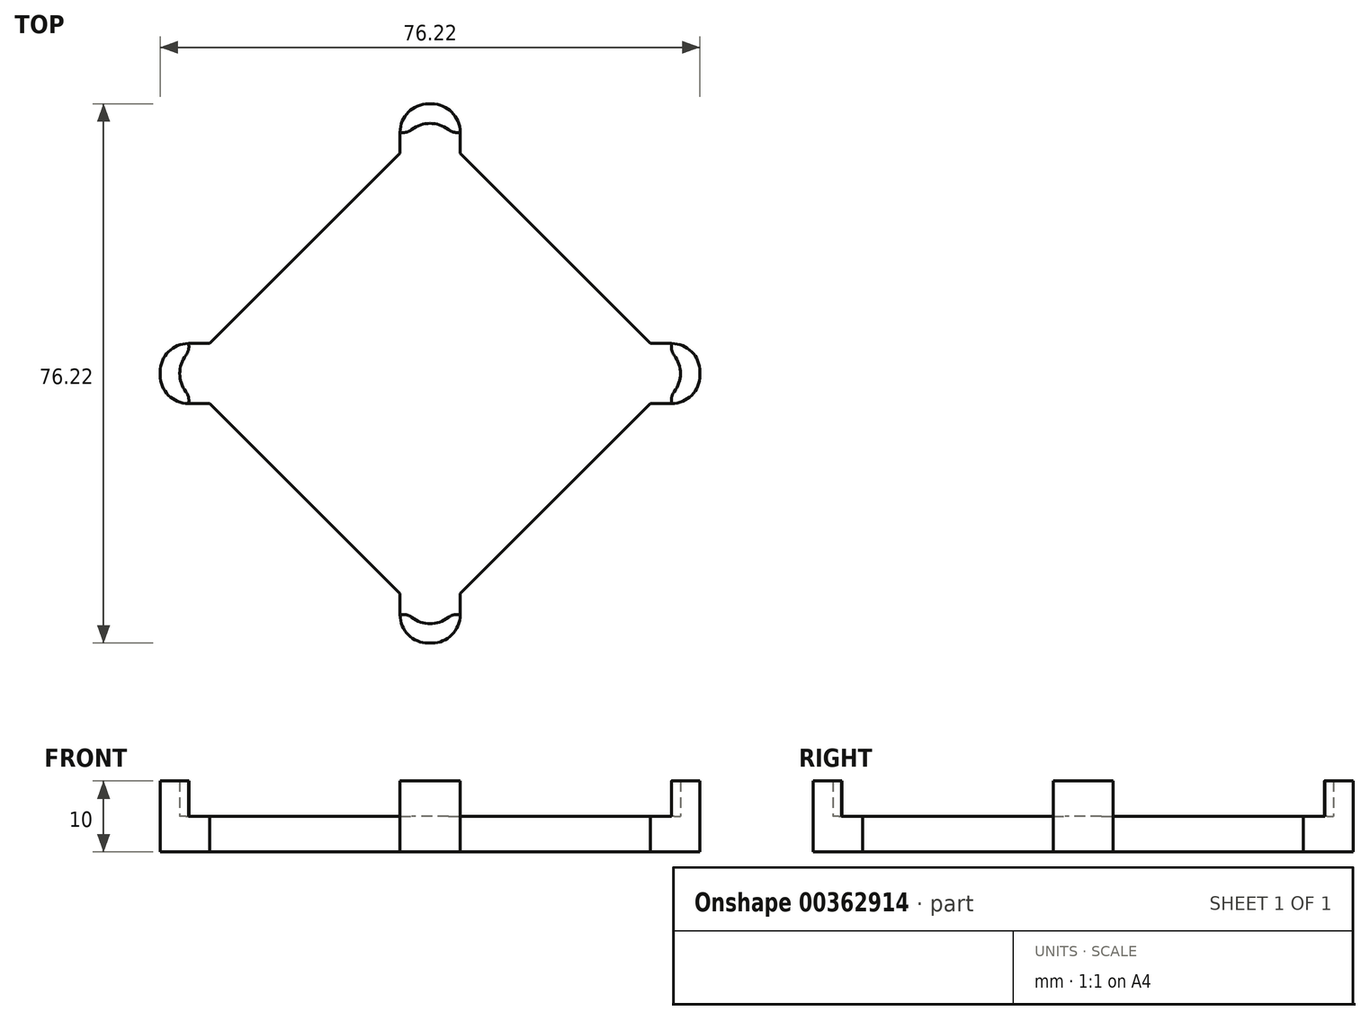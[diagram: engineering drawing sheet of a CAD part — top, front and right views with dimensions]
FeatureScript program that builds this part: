
annotation { "Feature Type Name" : "Feature", "Feature Type Description" : "" }
export const myFeature = defineFeature(function(context is Context, id is Id, definition is map)
    precondition{}
    {
        {
            var Q0;
            Q0=qCreatedBy(makeId("Top.planeOp"),FACE);
            var sketch = newSketch(context, id + "F0", { "sketchPlane" : qUnion([Q0])});
            skLineSegment(sketch, "E0", {"start": v(0, 35.36) * mm, "end": v(0, -35.36) * mm, "construction": true});
            skLineSegment(sketch, "E1", {"start": v(-35.36, 0) * mm, "end": v(35.36, 0) * mm, "construction": true});
            skPoint(sketch, "E2", {"position": v(0, 27.5) * mm});
            skPoint(sketch, "E3", {"position": v(-27.5, 0) * mm});
            skPoint(sketch, "E4", {"position": v(0, -27.5) * mm});
            skPoint(sketch, "E5", {"position": v(27.5, 0) * mm});
            skPoint(sketch, "E6", {"position": v(0, 0) * mm});
            skPoint(sketch, "E7", {"position": v(4.24, 31.11) * mm});
            skPoint(sketch, "E8", {"position": v(-4.24, 31.11) * mm});
            skPoint(sketch, "E9", {"position": v(-8.56, 26.8) * mm});
            skPoint(sketch, "E10", {"position": v(8.56, 26.8) * mm});
            skPoint(sketch, "E11", {"position": v(31.11, 4.24) * mm});
            skPoint(sketch, "E12", {"position": v(31.11, -4.24) * mm});
            skPoint(sketch, "E13", {"position": v(26.8, 8.56) * mm});
            skPoint(sketch, "E14", {"position": v(-31.11, -4.24) * mm});
            skPoint(sketch, "E15", {"position": v(-31.11, 4.24) * mm});
            skPoint(sketch, "E16", {"position": v(-26.8, 8.56) * mm});
            skPoint(sketch, "E17", {"position": v(4.24, -31.11) * mm});
            skPoint(sketch, "E18", {"position": v(-4.24, -31.11) * mm});
            skLineSegment(sketch, "E19", {"start": v(-31.11, 4.24) * mm, "end": v(-4.24, 31.11) * mm});
            skLineSegment(sketch, "E20", {"start": v(4.24, 31.11) * mm, "end": v(31.11, 4.24) * mm});
            skLineSegment(sketch, "E21", {"start": v(31.11, -4.24) * mm, "end": v(4.24, -31.11) * mm});
            skLineSegment(sketch, "E22", {"start": v(-4.24, -31.11) * mm, "end": v(-31.11, -4.24) * mm});
            skPoint(sketch, "E23", {"position": v(-17.68, -17.68) * mm});
            skPoint(sketch, "E24", {"position": v(17.68, -17.68) * mm});
            skPoint(sketch, "E25", {"position": v(17.68, 17.68) * mm});
            skPoint(sketch, "E26", {"position": v(-17.68, 17.68) * mm});
            skLineSegment(sketch, "E27", {"start": v(31.11, 4.24) * mm, "end": v(38.11, 4.24) * mm});
            skLineSegment(sketch, "E28", {"start": v(38.11, 4.24) * mm, "end": v(38.11, -4.24) * mm});
            skLineSegment(sketch, "E29", {"start": v(38.11, -4.24) * mm, "end": v(31.11, -4.24) * mm});
            skLineSegment(sketch, "E30", {"start": v(4.24, -31.11) * mm, "end": v(4.24, -38.11) * mm});
            skLineSegment(sketch, "E31", {"start": v(4.24, -38.11) * mm, "end": v(-4.24, -38.11) * mm});
            skLineSegment(sketch, "E32", {"start": v(-4.24, -38.11) * mm, "end": v(-4.24, -31.11) * mm});
            skLineSegment(sketch, "E33", {"start": v(-31.11, -4.24) * mm, "end": v(-38.11, -4.24) * mm});
            skLineSegment(sketch, "E34", {"start": v(-38.11, -4.24) * mm, "end": v(-38.11, 4.24) * mm});
            skLineSegment(sketch, "E35", {"start": v(-38.11, 4.24) * mm, "end": v(-31.11, 4.24) * mm});
            skLineSegment(sketch, "E36", {"start": v(-4.24, 31.11) * mm, "end": v(-4.24, 38.11) * mm});
            skLineSegment(sketch, "E37", {"start": v(-4.24, 38.11) * mm, "end": v(4.24, 38.11) * mm});
            skLineSegment(sketch, "E38", {"start": v(4.24, 38.11) * mm, "end": v(4.24, 31.11) * mm});
            skLineSegment(sketch, "E39", {"start": v(-4.24, -31.11) * mm, "end": v(4.24, -31.11) * mm});
            skLineSegment(sketch, "E40", {"start": v(31.11, -4.24) * mm, "end": v(31.11, 4.24) * mm});
            skLineSegment(sketch, "E41", {"start": v(4.24, 31.11) * mm, "end": v(-4.24, 31.11) * mm});
            skLineSegment(sketch, "E42", {"start": v(-31.11, 4.24) * mm, "end": v(-31.11, -4.24) * mm});
            skArc(sketch, "E43", {"start": v(-4.24, -31.11) * mm, "mid": v(0, -35.36) * mm, "end": v(4.24, -31.11) * mm});
            skArc(sketch, "E44", {"start": v(31.11, -4.24) * mm, "mid": v(35.36, 0) * mm, "end": v(31.11, 4.24) * mm});
            skArc(sketch, "E45", {"start": v(4.24, 31.11) * mm, "mid": v(0, 35.36) * mm, "end": v(-4.24, 31.11) * mm});
            skArc(sketch, "E46", {"start": v(-31.11, 4.24) * mm, "mid": v(-35.36, 0) * mm, "end": v(-31.11, -4.24) * mm});
            skSolve(sketch);
        }
        {
            var Q0;
            Q0=makeQuery(id+"F0.imprint","IMPRINT",FACE,{"disambiguationData":[TD([[makeQuery(id+"F0.imprint","IMPRINT",EDGE,{"derivedFrom":sQuery(id+"F0.wireOp",EDGE,"E39")}),-1.0]])]});
            var Q1;
            Q1=makeQuery(id+"F0.imprint","IMPRINT",FACE,{"disambiguationData":[TD([[makeQuery(id+"F0.imprint","IMPRINT",EDGE,{"derivedFrom":sQuery(id+"F0.wireOp",EDGE,"E19")}),-1.0]])]});
            var Q2;
            Q2=makeQuery(id+"F0.imprint","IMPRINT",FACE,{"disambiguationData":[TD([[makeQuery(id+"F0.imprint","IMPRINT",EDGE,{"derivedFrom":sQuery(id+"F0.wireOp",EDGE,"E42")}),-1.0]])]});
            var Q3;
            Q3=makeQuery(id+"F0.imprint","IMPRINT",FACE,{"disambiguationData":[TD([[makeQuery(id+"F0.imprint","IMPRINT",EDGE,{"derivedFrom":sQuery(id+"F0.wireOp",EDGE,"E40")}),-1.0]])]});
            var Q4;
            Q4=makeQuery(id+"F0.imprint","IMPRINT",FACE,{"disambiguationData":[TD([[makeQuery(id+"F0.imprint","IMPRINT",EDGE,{"derivedFrom":sQuery(id+"F0.wireOp",EDGE,"E27")}),-1.0]])]});
            var Q5;
            Q5=makeQuery(id+"F0.imprint","IMPRINT",FACE,{"disambiguationData":[TD([[makeQuery(id+"F0.imprint","IMPRINT",EDGE,{"derivedFrom":sQuery(id+"F0.wireOp",EDGE,"E30")}),-1.0]])]});
            var Q6;
            Q6=makeQuery(id+"F0.imprint","IMPRINT",FACE,{"disambiguationData":[TD([[makeQuery(id+"F0.imprint","IMPRINT",EDGE,{"derivedFrom":sQuery(id+"F0.wireOp",EDGE,"E33")}),-1.0]])]});
            var Q7;
            Q7=makeQuery(id+"F0.imprint","IMPRINT",FACE,{"disambiguationData":[TD([[makeQuery(id+"F0.imprint","IMPRINT",EDGE,{"derivedFrom":sQuery(id+"F0.wireOp",EDGE,"E41")}),-1.0]])]});
            var Q8;
            Q8=makeQuery(id+"F0.imprint","IMPRINT",FACE,{"disambiguationData":[TD([[makeQuery(id+"F0.imprint","IMPRINT",EDGE,{"derivedFrom":sQuery(id+"F0.wireOp",EDGE,"E36")}),-1.0]])]});
            extrude(context, id + "F1", {"entities" : qUnion([Q0, Q1, Q2, Q3, Q4, Q5, Q6, Q7, Q8]), "oppositeDirection" : true, "depth" : 5 * mm, "offsetDistance" : 25 * mm});
        }
        {
            var Q0;
            Q0=makeQuery(id+"F0.imprint","IMPRINT",FACE,{"disambiguationData":[TD([[makeQuery(id+"F0.imprint","IMPRINT",EDGE,{"derivedFrom":sQuery(id+"F0.wireOp",EDGE,"E33")}),-1.0]])]});
            var Q1;
            Q1=makeQuery(id+"F0.imprint","IMPRINT",FACE,{"disambiguationData":[TD([[makeQuery(id+"F0.imprint","IMPRINT",EDGE,{"derivedFrom":sQuery(id+"F0.wireOp",EDGE,"E30")}),-1.0]])]});
            var Q2;
            Q2=makeQuery(id+"F0.imprint","IMPRINT",FACE,{"disambiguationData":[TD([[makeQuery(id+"F0.imprint","IMPRINT",EDGE,{"derivedFrom":sQuery(id+"F0.wireOp",EDGE,"E36")}),-1.0]])]});
            var Q3;
            Q3=makeQuery(id+"F0.imprint","IMPRINT",FACE,{"disambiguationData":[TD([[makeQuery(id+"F0.imprint","IMPRINT",EDGE,{"derivedFrom":sQuery(id+"F0.wireOp",EDGE,"E27")}),-1.0]])]});
            extrude(context, id + "F2", {"entities" : qUnion([Q0, Q1, Q2, Q3]), "operationType" : NewBodyOperationType.ADD, "depth" : 5 * mm, "offsetDistance" : 25 * mm});
        }
        {
            var Q0;
            {var subQ0=sQuery(id+"F0.wireOp",EDGE,"E38");var subQ1=sQuery(id+"F0.wireOp",EDGE,"E37");Q0=makeQuery(id+"F2.boolean.opBoolean","MERGE",EDGE,{"derivedFrom":[makeQuery(id+"F1.opExtrude","SWEPT_EDGE",EDGE,{"disambiguationData":[OSD([subQ1,subQ0])]}),makeQuery(id+"F2.opExtrude","SWEPT_EDGE",EDGE,{"disambiguationData":[OSD([subQ1,subQ0])]})]});}
            var Q1;
            {var subQ0=sQuery(id+"F0.wireOp",EDGE,"E37");var subQ1=sQuery(id+"F0.wireOp",EDGE,"E36");Q1=makeQuery(id+"F2.boolean.opBoolean","MERGE",EDGE,{"derivedFrom":[makeQuery(id+"F1.opExtrude","SWEPT_EDGE",EDGE,{"disambiguationData":[OSD([subQ1,subQ0])]}),makeQuery(id+"F2.opExtrude","SWEPT_EDGE",EDGE,{"disambiguationData":[OSD([subQ1,subQ0])]})]});}
            var Q2;
            {var subQ0=sQuery(id+"F0.wireOp",EDGE,"E35");var subQ1=sQuery(id+"F0.wireOp",EDGE,"E34");Q2=makeQuery(id+"F2.boolean.opBoolean","MERGE",EDGE,{"derivedFrom":[makeQuery(id+"F1.opExtrude","SWEPT_EDGE",EDGE,{"disambiguationData":[OSD([subQ1,subQ0])]}),makeQuery(id+"F2.opExtrude","SWEPT_EDGE",EDGE,{"disambiguationData":[OSD([subQ1,subQ0])]})]});}
            var Q3;
            {var subQ0=sQuery(id+"F0.wireOp",EDGE,"E34");var subQ1=sQuery(id+"F0.wireOp",EDGE,"E33");Q3=makeQuery(id+"F2.boolean.opBoolean","MERGE",EDGE,{"derivedFrom":[makeQuery(id+"F1.opExtrude","SWEPT_EDGE",EDGE,{"disambiguationData":[OSD([subQ1,subQ0])]}),makeQuery(id+"F2.opExtrude","SWEPT_EDGE",EDGE,{"disambiguationData":[OSD([subQ1,subQ0])]})]});}
            var Q4;
            {var subQ0=sQuery(id+"F0.wireOp",EDGE,"E32");var subQ1=sQuery(id+"F0.wireOp",EDGE,"E31");Q4=makeQuery(id+"F2.boolean.opBoolean","MERGE",EDGE,{"derivedFrom":[makeQuery(id+"F1.opExtrude","SWEPT_EDGE",EDGE,{"disambiguationData":[OSD([subQ1,subQ0])]}),makeQuery(id+"F2.opExtrude","SWEPT_EDGE",EDGE,{"disambiguationData":[OSD([subQ1,subQ0])]})]});}
            var Q5;
            {var subQ0=sQuery(id+"F0.wireOp",EDGE,"E31");var subQ1=sQuery(id+"F0.wireOp",EDGE,"E30");Q5=makeQuery(id+"F2.boolean.opBoolean","MERGE",EDGE,{"derivedFrom":[makeQuery(id+"F1.opExtrude","SWEPT_EDGE",EDGE,{"disambiguationData":[OSD([subQ1,subQ0])]}),makeQuery(id+"F2.opExtrude","SWEPT_EDGE",EDGE,{"disambiguationData":[OSD([subQ1,subQ0])]})]});}
            var Q6;
            {var subQ0=sQuery(id+"F0.wireOp",EDGE,"E29");var subQ1=sQuery(id+"F0.wireOp",EDGE,"E28");Q6=makeQuery(id+"F2.boolean.opBoolean","MERGE",EDGE,{"derivedFrom":[makeQuery(id+"F1.opExtrude","SWEPT_EDGE",EDGE,{"disambiguationData":[OSD([subQ1,subQ0])]}),makeQuery(id+"F2.opExtrude","SWEPT_EDGE",EDGE,{"disambiguationData":[OSD([subQ1,subQ0])]})]});}
            var Q7;
            {var subQ0=sQuery(id+"F0.wireOp",EDGE,"E28");var subQ1=sQuery(id+"F0.wireOp",EDGE,"E27");Q7=makeQuery(id+"F2.boolean.opBoolean","MERGE",EDGE,{"derivedFrom":[makeQuery(id+"F1.opExtrude","SWEPT_EDGE",EDGE,{"disambiguationData":[OSD([subQ1,subQ0])]}),makeQuery(id+"F2.opExtrude","SWEPT_EDGE",EDGE,{"disambiguationData":[OSD([subQ1,subQ0])]})]});}
            fillet(context, id + "F3", {"entities" : qUnion([Q0, Q1, Q2, Q3, Q4, Q5, Q6, Q7]), "radius" : 4 * mm, "tangentPropagation" : true, "allowEdgeOverflow" : false});
        }
        {
            var Q0;
            Q0=makeQuery(id+"F2.opExtrude","SWEPT_EDGE",EDGE,{"disambiguationData":[OSD([sQuery(id+"F0.wireOp",EDGE,"E19"),sQuery(id+"F0.wireOp",EDGE,"E35"),sQuery(id+"F0.wireOp",EDGE,"E42"),sQuery(id+"F0.wireOp",EDGE,"E46")])]});
            var Q1;
            Q1=makeQuery(id+"F2.opExtrude","SWEPT_EDGE",EDGE,{"disambiguationData":[OSD([sQuery(id+"F0.wireOp",EDGE,"E22"),sQuery(id+"F0.wireOp",EDGE,"E33"),sQuery(id+"F0.wireOp",EDGE,"E42"),sQuery(id+"F0.wireOp",EDGE,"E46")])]});
            var Q2;
            Q2=makeQuery(id+"F2.opExtrude","SWEPT_EDGE",EDGE,{"disambiguationData":[OSD([sQuery(id+"F0.wireOp",EDGE,"E22"),sQuery(id+"F0.wireOp",EDGE,"E32"),sQuery(id+"F0.wireOp",EDGE,"E39"),sQuery(id+"F0.wireOp",EDGE,"E43")])]});
            var Q3;
            Q3=makeQuery(id+"F2.opExtrude","SWEPT_EDGE",EDGE,{"disambiguationData":[OSD([sQuery(id+"F0.wireOp",EDGE,"E21"),sQuery(id+"F0.wireOp",EDGE,"E30"),sQuery(id+"F0.wireOp",EDGE,"E39"),sQuery(id+"F0.wireOp",EDGE,"E43")])]});
            var Q4;
            Q4=makeQuery(id+"F2.opExtrude","SWEPT_EDGE",EDGE,{"disambiguationData":[OSD([sQuery(id+"F0.wireOp",EDGE,"E19"),sQuery(id+"F0.wireOp",EDGE,"E36"),sQuery(id+"F0.wireOp",EDGE,"E41"),sQuery(id+"F0.wireOp",EDGE,"E45")])]});
            var Q5;
            Q5=makeQuery(id+"F2.opExtrude","SWEPT_EDGE",EDGE,{"disambiguationData":[OSD([sQuery(id+"F0.wireOp",EDGE,"E20"),sQuery(id+"F0.wireOp",EDGE,"E38"),sQuery(id+"F0.wireOp",EDGE,"E41"),sQuery(id+"F0.wireOp",EDGE,"E45")])]});
            var Q6;
            Q6=makeQuery(id+"F2.opExtrude","SWEPT_EDGE",EDGE,{"disambiguationData":[OSD([sQuery(id+"F0.wireOp",EDGE,"E20"),sQuery(id+"F0.wireOp",EDGE,"E27"),sQuery(id+"F0.wireOp",EDGE,"E40"),sQuery(id+"F0.wireOp",EDGE,"E44")])]});
            var Q7;
            Q7=makeQuery(id+"F2.opExtrude","SWEPT_EDGE",EDGE,{"disambiguationData":[OSD([sQuery(id+"F0.wireOp",EDGE,"E21"),sQuery(id+"F0.wireOp",EDGE,"E29"),sQuery(id+"F0.wireOp",EDGE,"E40"),sQuery(id+"F0.wireOp",EDGE,"E44")])]});
            fillet(context, id + "F4", {"entities" : qUnion([Q0, Q1, Q2, Q3, Q4, Q5, Q6, Q7]), "radius" : 2 * mm, "tangentPropagation" : true, "allowEdgeOverflow" : false});
        }
    });
